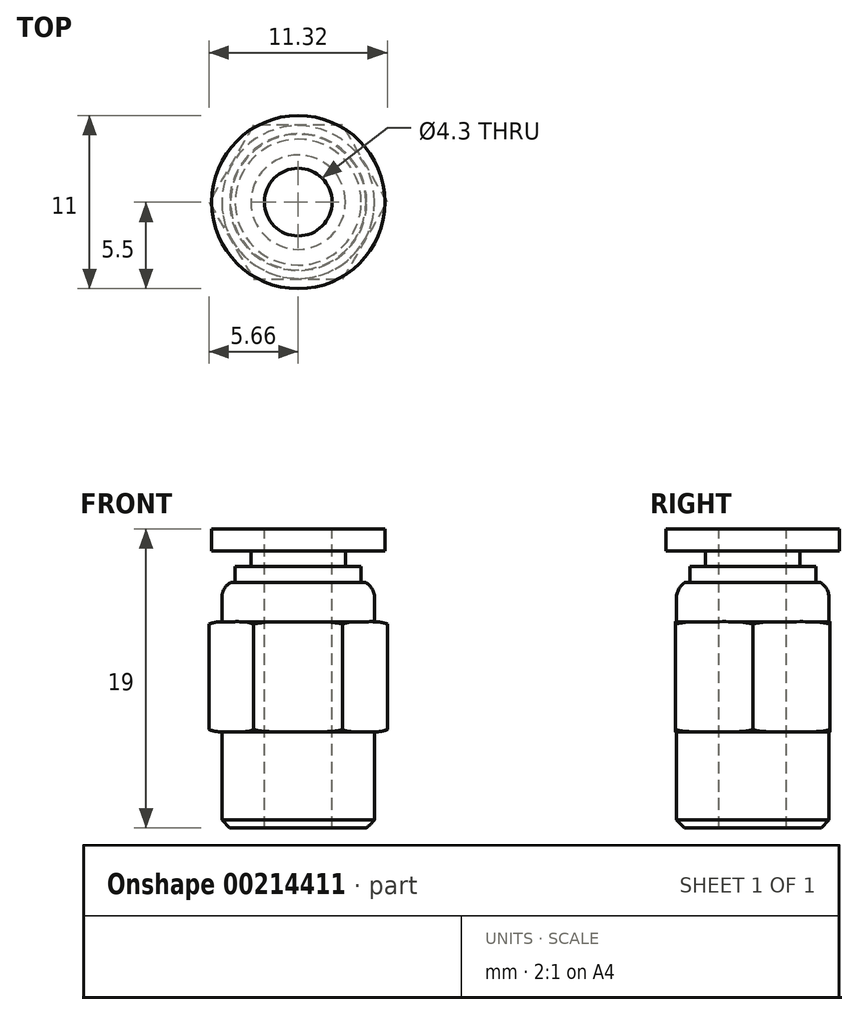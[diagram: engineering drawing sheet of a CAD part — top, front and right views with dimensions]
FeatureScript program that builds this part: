
annotation { "Feature Type Name" : "Feature", "Feature Type Description" : "" }
export const myFeature = defineFeature(function(context is Context, id is Id, definition is map)
    precondition{}
    {
        {
            var Q0;
            Q0=qCreatedBy(makeId("Front.planeOp"),FACE);
            var sketch = newSketch(context, id + "F0", { "sketchPlane" : qUnion([Q0])});
            skLineSegment(sketch, "E0", {"start": v(0, 0) * mm, "end": v(0, 19) * mm});
            skLineSegment(sketch, "E1", {"start": v(0, 19) * mm, "end": v(5.5, 19) * mm});
            skLineSegment(sketch, "E2", {"start": v(5.5, 19) * mm, "end": v(5.5, 17.6) * mm});
            skLineSegment(sketch, "E3", {"start": v(5.5, 17.6) * mm, "end": v(3, 17.6) * mm});
            skLineSegment(sketch, "E4", {"start": v(3, 17.6) * mm, "end": v(3, 16.6) * mm});
            skLineSegment(sketch, "E5", {"start": v(3, 16.6) * mm, "end": v(4, 16.6) * mm});
            skLineSegment(sketch, "E6", {"start": v(4, 16.6) * mm, "end": v(4, 15.6) * mm});
            skLineSegment(sketch, "E7", {"start": v(4, 15.6) * mm, "end": v(4.3, 15.6) * mm});
            skLineSegment(sketch, "E8", {"start": v(4.85, 14.6) * mm, "end": v(4.85, 13.1) * mm});
            skLineSegment(sketch, "E9", {"start": v(7, 11.6) * mm, "end": v(7, 7.6) * mm});
            skLineSegment(sketch, "E10", {"start": v(4.85, 6.1) * mm, "end": v(4.85, 0) * mm});
            skLineSegment(sketch, "E11", {"start": v(4.85, 0) * mm, "end": v(0, 0) * mm});
            skLineSegment(sketch, "E12", {"start": v(7, 9.6) * mm, "end": v(0, 9.6) * mm, "construction": true});
            skPoint(sketch, "E13.end.orphan", {"position": v(7, 13.1) * mm});
            skLineSegment(sketch, "E14", {"start": v(4.85, 13.1) * mm, "end": v(0, 13.1) * mm, "construction": true});
            skLineSegment(sketch, "E15", {"start": v(4.85, 6.1) * mm, "end": v(0, 6.1) * mm, "construction": true});
            skArc(sketch, "E16", {"start": v(7, 11.6) * mm, "mid": v(6.16, 12.69) * mm, "end": v(4.85, 13.1) * mm});
            skArc(sketch, "E17", {"start": v(4.85, 6.1) * mm, "mid": v(6.16, 6.51) * mm, "end": v(7, 7.6) * mm});
            skPoint(sketch, "E18.start.orphan", {"position": v(7, 6.1) * mm});
            skPoint(sketch, "E19.orphan", {"position": v(4.85, 15.6) * mm});
            skArc(sketch, "E20", {"start": v(4.85, 14.6) * mm, "mid": v(4.7, 15.17) * mm, "end": v(4.3, 15.6) * mm});
            skSolve(sketch);
        }
        {
            var Q0;
            Q0 = qSketchRegion(id + "F0", true);
            var Q1;
            Q1=sQuery(id+"F0.wireOp",EDGE,"E0");
            revolve(context, id + "F1", {"entities" : qUnion([Q0]), "axis" : qUnion([Q1]), "revolveType" : RevolveType.FULL});
        }
        {
            var Q0;
            Q0=makeQuery(id+"F1.opRevolve","SWEPT_FACE",FACE,{"disambiguationData":[OSD([sQuery(id+"F0.wireOp",EDGE,"E1")])]});
            var sketch = newSketch(context, id + "F2", { "sketchPlane" : qUnion([Q0])});
            skCircle(sketch, "E21", {"center": v(0, 0) * mm, "radius": 2.15 * mm});
            skSolve(sketch);
        }
        {
            var Q0;
            Q0 = qSketchRegion(id + "F2", true);
            extrude(context, id + "F3", {"entities" : qUnion([Q0]), "operationType" : NewBodyOperationType.REMOVE, "endBound" : BoundingType.THROUGH_ALL, "oppositeDirection" : true, "depth" : 25 * mm});
        }
        {
            var Q0;
            Q0=makeQuery(id+"F1.opRevolve","SWEPT_FACE",FACE,{"disambiguationData":[OSD([sQuery(id+"F0.wireOp",EDGE,"E11")])]});
            var sketch = newSketch(context, id + "F4", { "sketchPlane" : qUnion([Q0])});
            skCircle(sketch, "E22.cCircle", {"center": v(0, 0) * mm, "radius": 4.9 * mm, "construction": true});
            skLineSegment(sketch, "E22.0", {"start": v(2.83, 4.9) * mm, "end": v(5.66, 0) * mm});
            skLineSegment(sketch, "E22.1", {"start": v(5.66, 0) * mm, "end": v(2.83, -4.9) * mm});
            skLineSegment(sketch, "E22.2", {"start": v(2.83, -4.9) * mm, "end": v(-2.83, -4.9) * mm});
            skLineSegment(sketch, "E22.3", {"start": v(-2.83, -4.9) * mm, "end": v(-5.66, 0) * mm});
            skLineSegment(sketch, "E22.4", {"start": v(-5.66, 0) * mm, "end": v(-2.83, 4.9) * mm});
            skLineSegment(sketch, "E22.5", {"start": v(-2.83, 4.9) * mm, "end": v(2.83, 4.9) * mm});
            skPoint(sketch, "E22.0.midPoint", {"position": v(4.24, 2.45) * mm});
            skLineSegment(sketch, "E23", {"start": v(0, 0) * mm, "end": v(-5.66, 0) * mm, "construction": true});
            skCircle(sketch, "E24", {"center": v(0, 0) * mm, "radius": 9 * mm});
            skSolve(sketch);
        }
        {
            var Q0;
            Q0 = qSketchRegion(id + "F4", true);
            extrude(context, id + "F5", {"entities" : qUnion([Q0]), "operationType" : NewBodyOperationType.REMOVE, "oppositeDirection" : true, "depth" : 14 * mm});
        }
        {
            var Q0;
            Q0=makeQuery(id+"F1.opRevolve","SWEPT_EDGE",EDGE,{"disambiguationData":[OSD([sQuery(id+"F0.wireOp",EDGE,"E10"),sQuery(id+"F0.wireOp",EDGE,"E11")])]});
            chamfer(context, id + "F6", {"entities" : qUnion([Q0]), "width" : 0.5 * mm, "tangentPropagation" : true});
        }
    });
